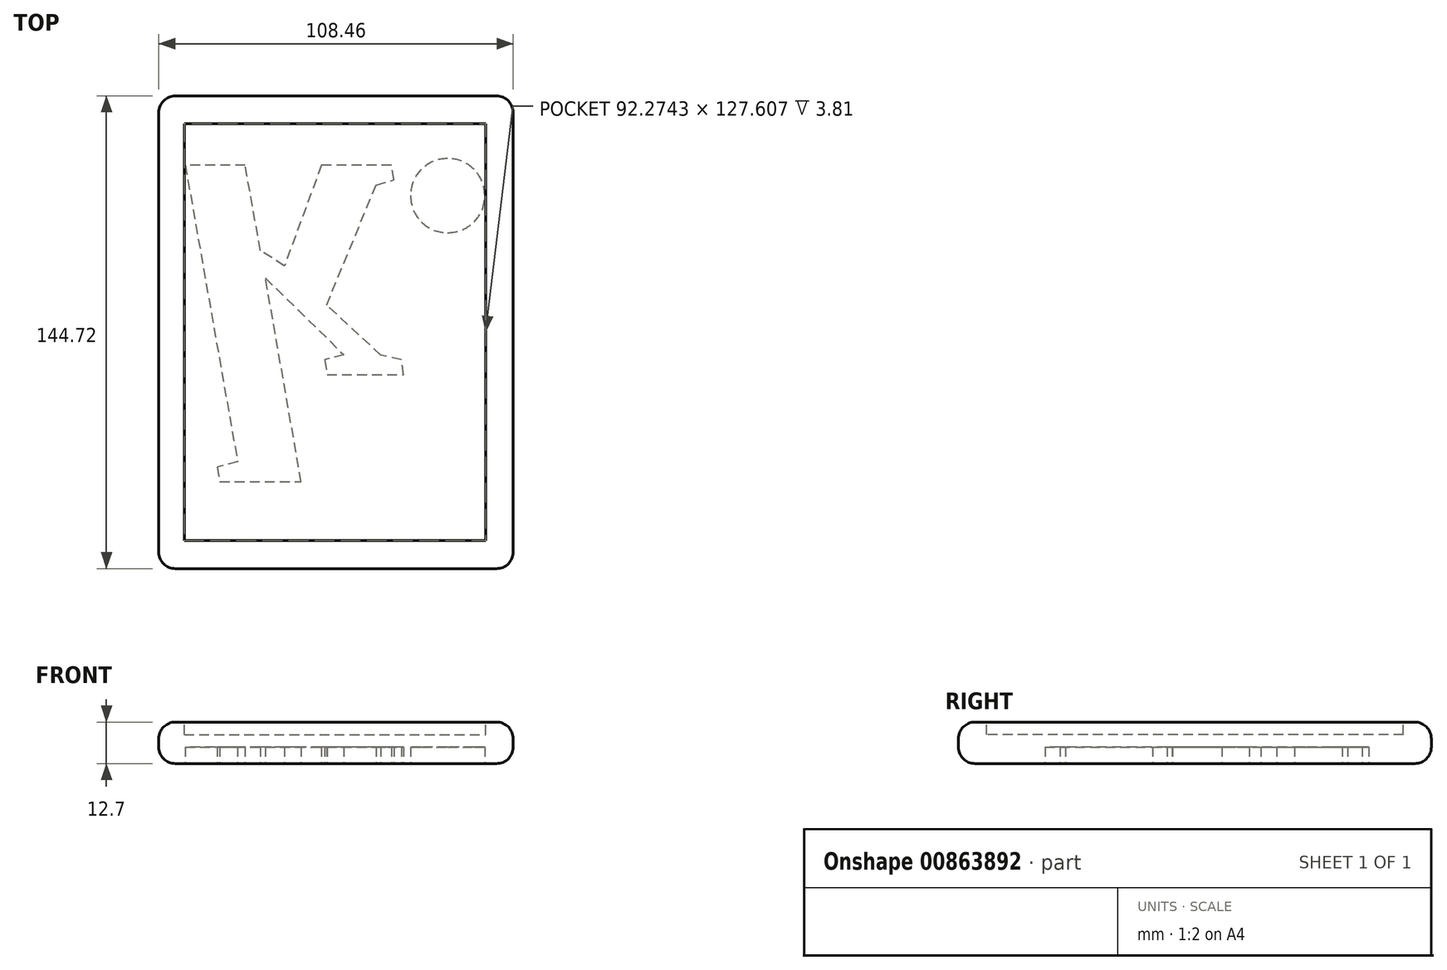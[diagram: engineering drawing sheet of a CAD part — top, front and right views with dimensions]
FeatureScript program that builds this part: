
annotation { "Feature Type Name" : "Feature", "Feature Type Description" : "" }
export const myFeature = defineFeature(function(context is Context, id is Id, definition is map)
    precondition{}
    {
        {
            var Q0;
            Q0=qCreatedBy(makeId("Top.planeOp"),FACE);
            var sketch = newSketch(context, id + "F0", { "sketchPlane" : qUnion([Q0])});
            skLineSegment(sketch, "E0.bottom", {"start": v(-53.18, 72.05) * mm, "end": v(55.28, 72.05) * mm});
            skLineSegment(sketch, "E0.top", {"start": v(-53.18, -72.67) * mm, "end": v(55.28, -72.67) * mm});
            skLineSegment(sketch, "E0.left", {"start": v(-53.18, 72.05) * mm, "end": v(-53.18, -72.67) * mm});
            skLineSegment(sketch, "E0.right", {"start": v(55.28, 72.05) * mm, "end": v(55.28, -72.67) * mm});
            skSolve(sketch);
        }
        {
            var Q0;
            Q0 = qSketchRegion(id + "F0", true);
            extrude(context, id + "F1", {"entities" : qUnion([Q0]), "depth" : 12.7 * mm, "offsetDistance" : 25.4 * mm});
        }
        {
            var Q0;
            Q0=makeQuery(id+"F1.opExtrude","CAP_FACE",FACE,{"disambiguationData":[OSD([sQuery(id+"F0.wireOp",EDGE,"E0.bottom"),sQuery(id+"F0.wireOp",EDGE,"E0.top"),sQuery(id+"F0.wireOp",EDGE,"E0.left"),sQuery(id+"F0.wireOp",EDGE,"E0.right")])],"isStart":false});
            var sketch = newSketch(context, id + "F2", { "sketchPlane" : qUnion([Q0])});
            skLineSegment(sketch, "E1.bottom", {"start": v(-45.4, 63.51) * mm, "end": v(46.87, 63.51) * mm});
            skLineSegment(sketch, "E1.top", {"start": v(-45.4, -64.1) * mm, "end": v(46.87, -64.1) * mm});
            skLineSegment(sketch, "E1.left", {"start": v(-45.4, 63.51) * mm, "end": v(-45.4, -64.1) * mm});
            skLineSegment(sketch, "E1.right", {"start": v(46.87, 63.51) * mm, "end": v(46.87, -64.1) * mm});
            skSolve(sketch);
        }
        {
            var Q0;
            Q0 = qSketchRegion(id + "F2", true);
            extrude(context, id + "F3", {"entities" : qUnion([Q0]), "operationType" : NewBodyOperationType.REMOVE, "endBound" : BoundingType.SYMMETRIC, "oppositeDirection" : true, "depth" : 7.62 * mm, "offsetDistance" : 25.4 * mm});
        }
        {
            var Q0;
            Q0=makeQuery(id+"F1.opExtrude","CAP_EDGE",EDGE,{"disambiguationData":[OSD([sQuery(id+"F0.wireOp",EDGE,"E0.bottom")])],"isStart":false});
            var Q1;
            Q1=makeQuery(id+"F1.opExtrude","CAP_EDGE",EDGE,{"disambiguationData":[OSD([sQuery(id+"F0.wireOp",EDGE,"E0.left")])],"isStart":false});
            var Q2;
            Q2=makeQuery(id+"F1.opExtrude","CAP_EDGE",EDGE,{"disambiguationData":[OSD([sQuery(id+"F0.wireOp",EDGE,"E0.right")])],"isStart":false});
            var Q3;
            Q3=makeQuery(id+"F1.opExtrude","CAP_EDGE",EDGE,{"disambiguationData":[OSD([sQuery(id+"F0.wireOp",EDGE,"E0.top")])],"isStart":false});
            fillet(context, id + "F4", {"entities" : qUnion([Q0, Q1, Q2, Q3]), "radius" : 5.08 * mm, "tangentPropagation" : true, "allowEdgeOverflow" : false});
        }
        {
            var Q0;
            Q0=makeQuery(id+"F1.opExtrude","SWEPT_EDGE",EDGE,{"disambiguationData":[OSD([sQuery(id+"F0.wireOp",EDGE,"E0.bottom"),sQuery(id+"F0.wireOp",EDGE,"E0.left")])]});
            var Q1;
            Q1=makeQuery(id+"F1.opExtrude","SWEPT_EDGE",EDGE,{"disambiguationData":[OSD([sQuery(id+"F0.wireOp",EDGE,"E0.top"),sQuery(id+"F0.wireOp",EDGE,"E0.right")])]});
            var Q2;
            Q2=makeQuery(id+"F1.opExtrude","SWEPT_EDGE",EDGE,{"disambiguationData":[OSD([sQuery(id+"F0.wireOp",EDGE,"E0.bottom"),sQuery(id+"F0.wireOp",EDGE,"E0.right")])]});
            var Q3;
            Q3=makeQuery(id+"F1.opExtrude","SWEPT_EDGE",EDGE,{"disambiguationData":[OSD([sQuery(id+"F0.wireOp",EDGE,"E0.top"),sQuery(id+"F0.wireOp",EDGE,"E0.left")])]});
            fillet(context, id + "F5", {"entities" : qUnion([Q0, Q1, Q2, Q3]), "radius" : 5.08 * mm, "tangentPropagation" : true, "allowEdgeOverflow" : false});
        }
        {
            var Q0;
            Q0=makeQuery(id+"F1.opExtrude","CAP_FACE",FACE,{"disambiguationData":[OSD([sQuery(id+"F0.wireOp",EDGE,"E0.bottom"),sQuery(id+"F0.wireOp",EDGE,"E0.top"),sQuery(id+"F0.wireOp",EDGE,"E0.left"),sQuery(id+"F0.wireOp",EDGE,"E0.right")])],"isStart":true});
            var sketch = newSketch(context, id + "F6", { "sketchPlane" : qUnion([Q0])});
            skText(sketch, "E2", { "text": "k. ", "fontName": "Tinos-BoldItalic.ttf"});
            const initialGuessF6  = {"E2": [-0.04702, -0.05089, 1, 0, 0.10064]};
            skSetInitialGuess(sketch, initialGuessF6);
            skSolve(sketch);
        }
        {
            var Q0;
            Q0=makeQuery(id+"F6.imprint","IMPRINT",FACE,{"disambiguationData":[TD([[makeQuery(id+"F6.imprint","IMPRINT",EDGE,{"derivedFrom":sQuery(id+"F6.wireOp",EDGE,"E2.sketch_text.stroke-0")}),-1.0]])]});
            extrude(context, id + "F7", {"entities" : qUnion([Q0]), "operationType" : NewBodyOperationType.REMOVE, "oppositeDirection" : true, "depth" : 5.08 * mm, "offsetDistance" : 25.4 * mm});
        }
        {
            var Q0;
            Q0=makeQuery(id+"F6.imprint","IMPRINT",FACE,{"disambiguationData":[TD([[makeQuery(id+"F6.imprint","IMPRINT",EDGE,{"derivedFrom":sQuery(id+"F6.wireOp",EDGE,"E2.sketch_text.stroke-20")}),-1.0]])]});
            extrude(context, id + "F8", {"entities" : qUnion([Q0]), "operationType" : NewBodyOperationType.REMOVE, "oppositeDirection" : true, "depth" : 5.08 * mm, "offsetDistance" : 25.4 * mm});
        }
        {
            var Q0;
            {var subQ0=sQuery(id+"F0.wireOp",EDGE,"E0.left");var subQ1=sQuery(id+"F0.wireOp",EDGE,"E0.top");Q0=makeQuery(id+"F5.opFillet","BLEND_EDGE",EDGE,{"blendedFrom":[makeQuery(id+"F1.opExtrude","SWEPT_EDGE",EDGE,{"disambiguationData":[OSD([subQ1,subQ0])]}),makeQuery(id+"F1.opExtrude","CAP_FACE",FACE,{"disambiguationData":[OSD([sQuery(id+"F0.wireOp",EDGE,"E0.bottom"),subQ1,subQ0,sQuery(id+"F0.wireOp",EDGE,"E0.right")])],"isStart":true})],"blendedInto":[makeQuery(id+"F1.opExtrude","CAP_FACE",FACE,{"disambiguationData":[OSD([sQuery(id+"F0.wireOp",EDGE,"E0.bottom"),subQ1,subQ0,sQuery(id+"F0.wireOp",EDGE,"E0.right")])],"isStart":true})]});}
            fillet(context, id + "F9", {"entities" : qUnion([Q0]), "radius" : 5.08 * mm, "tangentPropagation" : true, "allowEdgeOverflow" : false});
        }
    });
